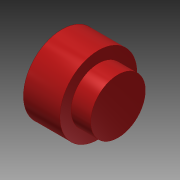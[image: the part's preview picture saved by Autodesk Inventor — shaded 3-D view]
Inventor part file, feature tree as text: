
AUTODESK INVENTOR PART (.ipt)
format: ipt  version: 2014 (Build 180170000, 170)  size: 89,600 bytes
history: native  units: mm
features: extrude x2, sketch x2, other x1
ambient origin geometry x8: Origin, YZ Plane, XZ Plane, XY Plane, X Axis, Y Axis, Z Axis, Center Point
bodies: Body1 (feature_tree)
feature tree (5):
  other  "Твердое тело1"
  extrude  "Выдавливание1"  Depth=11.0mm
  extrude  "Выдавливание2"  Depth=5.2mm TaperAngle=0.0deg
  sketch  "Эскиз1"
  sketch  "Эскиз2"
